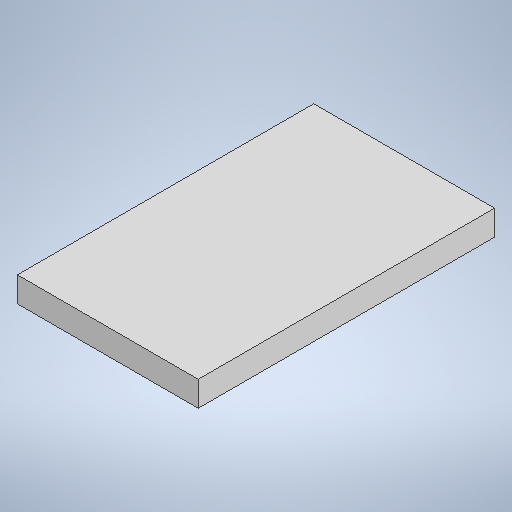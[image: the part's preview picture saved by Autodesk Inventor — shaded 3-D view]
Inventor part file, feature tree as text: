
AUTODESK INVENTOR PART (.ipt)
format: ipt  version: 2025.2 (Build 292293000, 293)  size: 207,360 bytes
history: native  units: mm
features: extrude x1, sketch x1
ambient origin geometry x8: Origin, YZ Plane, XZ Plane, XY Plane, X Axis, Y Axis, Z Axis, Center Point
bodies: Solid1 (feature_tree)
feature tree (2):
  extrude  "Extrusion1"  Depth=59.0mm
  sketch  "Sketch1"  dims[d0=36.0mm d1=59.0mm d2=5.0mm d3=0.0mm]
